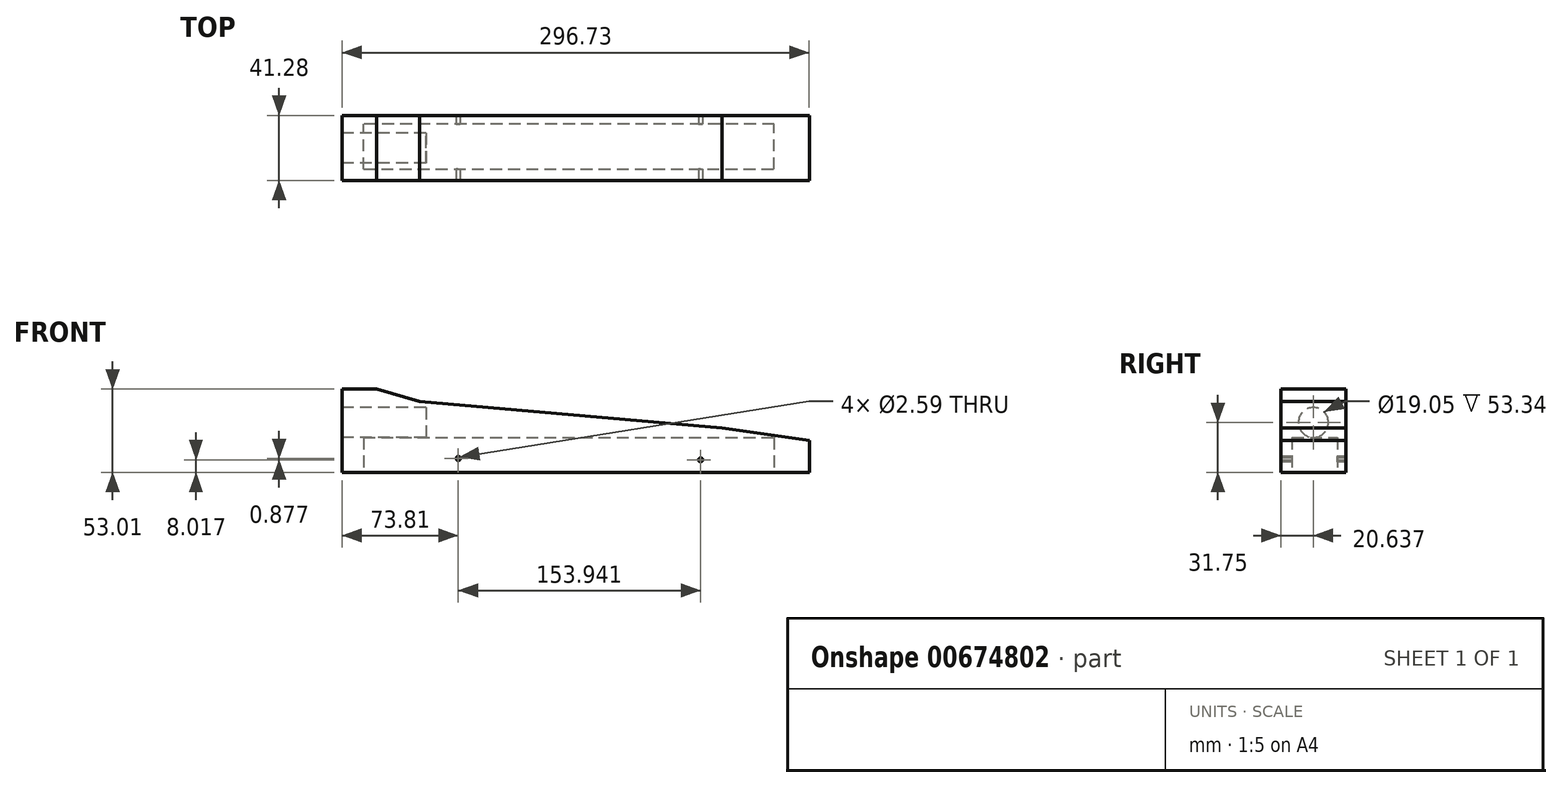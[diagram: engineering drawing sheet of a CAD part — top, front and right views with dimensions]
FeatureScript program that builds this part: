
annotation { "Feature Type Name" : "Feature", "Feature Type Description" : "" }
export const myFeature = defineFeature(function(context is Context, id is Id, definition is map)
    precondition{}
    {
        {
            var Q0;
            Q0=qCreatedBy(makeId("Front.planeOp"),FACE);
            var sketch = newSketch(context, id + "F0", { "sketchPlane" : qUnion([Q0])});
            skLineSegment(sketch, "E0", {"start": v(-73.81, 0) * mm, "end": v(222.92, 0) * mm});
            skLineSegment(sketch, "E1", {"start": v(-73.81, 0) * mm, "end": v(-73.81, 63.5) * mm});
            skLineSegment(sketch, "E2", {"start": v(222.92, 0) * mm, "end": v(222.92, 20.32) * mm});
            skLineSegment(sketch, "E3", {"start": v(-73.81, 63.5) * mm, "end": v(222.92, 20.32) * mm});
            skSolve(sketch);
        }
        {
            var Q0;
            Q0=makeQuery(id+"F0.imprint","IMPRINT",FACE,{"disambiguationData":[TD([[makeQuery(id+"F0.imprint","IMPRINT",EDGE,{"derivedFrom":sQuery(id+"F0.wireOp",EDGE,"E0")}),1.0]])]});
            extrude(context, id + "F1", {"entities" : qUnion([Q0]), "oppositeDirection" : true, "depth" : 41.27 * mm, "offsetDistance" : 25.4 * mm});
        }
        {
            var Q0;
            Q0=makeQuery(id+"F1.opExtrude","SWEPT_FACE",FACE,{"disambiguationData":[OSD([sQuery(id+"F0.wireOp",EDGE,"E1")])]});
            var sketch = newSketch(context, id + "F2", { "sketchPlane" : qUnion([Q0])});
            skCircle(sketch, "E4", {"center": v(-20.64, 31.75) * mm, "radius": 9.53 * mm});
            skPoint(sketch, "E4.centerSnap0", {"position": v(0, 31.75) * mm});
            skPoint(sketch, "E4.centerSnap1", {"position": v(-20.64, 63.5) * mm});
            skSolve(sketch);
        }
        {
            var Q0;
            Q0=makeQuery(id+"F2.imprint","IMPRINT",FACE,{"disambiguationData":[TD([[makeQuery(id+"F2.imprint","IMPRINT",EDGE,{"derivedFrom":sQuery(id+"F2.wireOp",EDGE,"E4")}),1.0]])]});
            extrude(context, id + "F3", {"entities" : qUnion([Q0]), "operationType" : NewBodyOperationType.REMOVE, "oppositeDirection" : true, "depth" : 53.34 * mm, "offsetDistance" : 25.4 * mm});
        }
        {
            var Q0;
            Q0=makeQuery(id+"F1.opExtrude","SWEPT_FACE",FACE,{"disambiguationData":[OSD([sQuery(id+"F0.wireOp",EDGE,"E0")])]});
            var sketch = newSketch(context, id + "F4", { "sketchPlane" : qUnion([Q0])});
            skSolve(sketch);
        }
        {
            var Q0;
            {var subQ0=sQuery(id+"F0.wireOp",EDGE,"E0");Q0=makeQuery(id+"F4.imprint","IMPRINT",FACE,{"disambiguationData":[TD([[makeQuery(id+"F4.imprint","IMPRINT",EDGE,{"derivedFrom":makeQuery(id+"F1.opExtrude","CAP_EDGE",EDGE,{"disambiguationData":[OSD([subQ0])],"isStart":true})}),-1.0]])]});}
            var sketch = newSketch(context, id + "F5", { "sketchPlane" : qUnion([Q0])});
            skLineSegment(sketch, "E5", {"start": v(-60.28, -7.04) * mm, "end": v(-60.28, -35.88) * mm});
            skLineSegment(sketch, "E6", {"start": v(-60.28, -7.04) * mm, "end": v(200.65, -7.04) * mm});
            skLineSegment(sketch, "E7", {"start": v(200.65, -7.04) * mm, "end": v(200.65, -35.88) * mm});
            skLineSegment(sketch, "E8", {"start": v(200.65, -35.88) * mm, "end": v(-60.28, -35.88) * mm});
            skSolve(sketch);
        }
        {
            var Q0;
            Q0=makeQuery(id+"F5.imprint","IMPRINT",FACE,{"disambiguationData":[TD([[makeQuery(id+"F5.imprint","IMPRINT",EDGE,{"derivedFrom":sQuery(id+"F5.wireOp",EDGE,"E5")}),1.0]])]});
            extrude(context, id + "F6", {"entities" : qUnion([Q0]), "operationType" : NewBodyOperationType.REMOVE, "oppositeDirection" : true, "depth" : 22.2 * mm, "offsetDistance" : 25.4 * mm});
        }
        {
            var Q0;
            Q0=makeQuery(id+"F1.opExtrude","CAP_FACE",FACE,{"disambiguationData":[OSD([sQuery(id+"F0.wireOp",EDGE,"E0"),sQuery(id+"F0.wireOp",EDGE,"E1"),sQuery(id+"F0.wireOp",EDGE,"E2"),sQuery(id+"F0.wireOp",EDGE,"E3")])],"isStart":true});
            var sketch = newSketch(context, id + "F7", { "sketchPlane" : qUnion([Q0])});
            skLineSegment(sketch, "E9", {"start": v(-39.23, 0) * mm, "end": v(-73.81, 16.7) * mm});
            skLineSegment(sketch, "E10", {"start": v(-73.81, 16.7) * mm, "end": v(-66.76, 20.93) * mm});
            skLineSegment(sketch, "E11", {"start": v(-66.76, 20.93) * mm, "end": v(-73.81, 25.25) * mm});
            skLineSegment(sketch, "E12", {"start": v(-73.81, 25.25) * mm, "end": v(-73.81, 53.01) * mm});
            skLineSegment(sketch, "E13", {"start": v(-73.81, 53.01) * mm, "end": v(-52, 53.01) * mm});
            skLineSegment(sketch, "E14", {"start": v(-52, 53.01) * mm, "end": v(-24.66, 45.21) * mm});
            skLineSegment(sketch, "E15", {"start": v(-24.66, 45.21) * mm, "end": v(167.5, 28.39) * mm});
            skLineSegment(sketch, "E16", {"start": v(167.5, 28.39) * mm, "end": v(167.5, 0) * mm});
            skLineSegment(sketch, "E17", {"start": v(167.5, 0) * mm, "end": v(-39.23, 0) * mm});
            skSolve(sketch);
        }
        {
            var Q0;
            {var subQ3=sQuery(id+"F7.wireOp",EDGE,"E13");Q0=makeQuery(id+"F7.imprint","IMPRINT",FACE,{"disambiguationData":[TD([[makeQuery(id+"F7.imprint","IMPRINT",EDGE,{"derivedFrom":subQ3}),1.0]])]});}
            extrude(context, id + "F8", {"entities" : qUnion([Q0]), "operationType" : NewBodyOperationType.REMOVE, "oppositeDirection" : true, "depth" : 50.8 * mm, "offsetDistance" : 25.4 * mm});
        }
        {
            var Q0;
            Q0=makeQuery(id+"F1.opExtrude","CAP_FACE",FACE,{"disambiguationData":[OSD([sQuery(id+"F0.wireOp",EDGE,"E0"),sQuery(id+"F0.wireOp",EDGE,"E1"),sQuery(id+"F0.wireOp",EDGE,"E2"),sQuery(id+"F0.wireOp",EDGE,"E3")])],"isStart":true});
            var sketch = newSketch(context, id + "F9", { "sketchPlane" : qUnion([Q0])});
            skCircle(sketch, "E18", {"center": v(169.94, 8.38) * mm, "radius": 3.7 * mm});
            skCircle(sketch, "E19", {"center": v(0, 8.9) * mm, "radius": 1.3 * mm});
            skSolve(sketch);
        }
        {
            var Q0;
            Q0=makeQuery(id+"F9.imprint","IMPRINT",FACE,{"disambiguationData":[TD([[makeQuery(id+"F9.imprint","IMPRINT",EDGE,{"derivedFrom":sQuery(id+"F9.wireOp",EDGE,"E19")}),1.0]])]});
            extrude(context, id + "F10", {"entities" : qUnion([Q0]), "operationType" : NewBodyOperationType.REMOVE, "oppositeDirection" : true, "depth" : 101.6 * mm, "offsetDistance" : 25.4 * mm});
        }
        {
            var Q0;
            Q0=makeQuery(id+"F1.opExtrude","CAP_FACE",FACE,{"disambiguationData":[OSD([sQuery(id+"F0.wireOp",EDGE,"E0"),sQuery(id+"F0.wireOp",EDGE,"E1"),sQuery(id+"F0.wireOp",EDGE,"E2"),sQuery(id+"F0.wireOp",EDGE,"E3")])],"isStart":true});
            var sketch = newSketch(context, id + "F11", { "sketchPlane" : qUnion([Q0])});
            skCircle(sketch, "E20", {"center": v(153.94, 8.02) * mm, "radius": 1.3 * mm});
            skSolve(sketch);
        }
        {
            var Q0;
            Q0=makeQuery(id+"F11.imprint","IMPRINT",FACE,{"disambiguationData":[TD([[makeQuery(id+"F11.imprint","IMPRINT",EDGE,{"derivedFrom":sQuery(id+"F11.wireOp",EDGE,"E20")}),1.0]])]});
            extrude(context, id + "F12", {"entities" : qUnion([Q0]), "operationType" : NewBodyOperationType.REMOVE, "oppositeDirection" : true, "depth" : 101.6 * mm, "offsetDistance" : 25.4 * mm});
        }
    });
